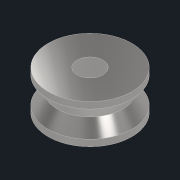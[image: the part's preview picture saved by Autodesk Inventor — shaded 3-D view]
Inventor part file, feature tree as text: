
AUTODESK INVENTOR PART (.ipt)
format: ipt  version: 2021.3 (Build 253353000, 353)  size: 105,472 bytes
history: native  units: mm
features: revolve x1, sketch x1
ambient origin geometry x8: Origin, YZ Plane, XZ Plane, XY Plane, X Axis, Y Axis, Z Axis, Center Point
bodies: Solid1 (feature_tree)
feature tree (2):
  revolve  "Revolution1"  [1 undecoded]
  sketch  "Sketch1"  dims[d0=2.0mm d1=6.06mm d2=3.03mm d3=4.5mm d5=1.0mm d6=5.1mm d7=90.0deg]
note: 1 required parameter value undecoded (feature->parameter linkage not recoverable at this tier; creation-order binding heuristic only, values carry confidence <= 0.55)
